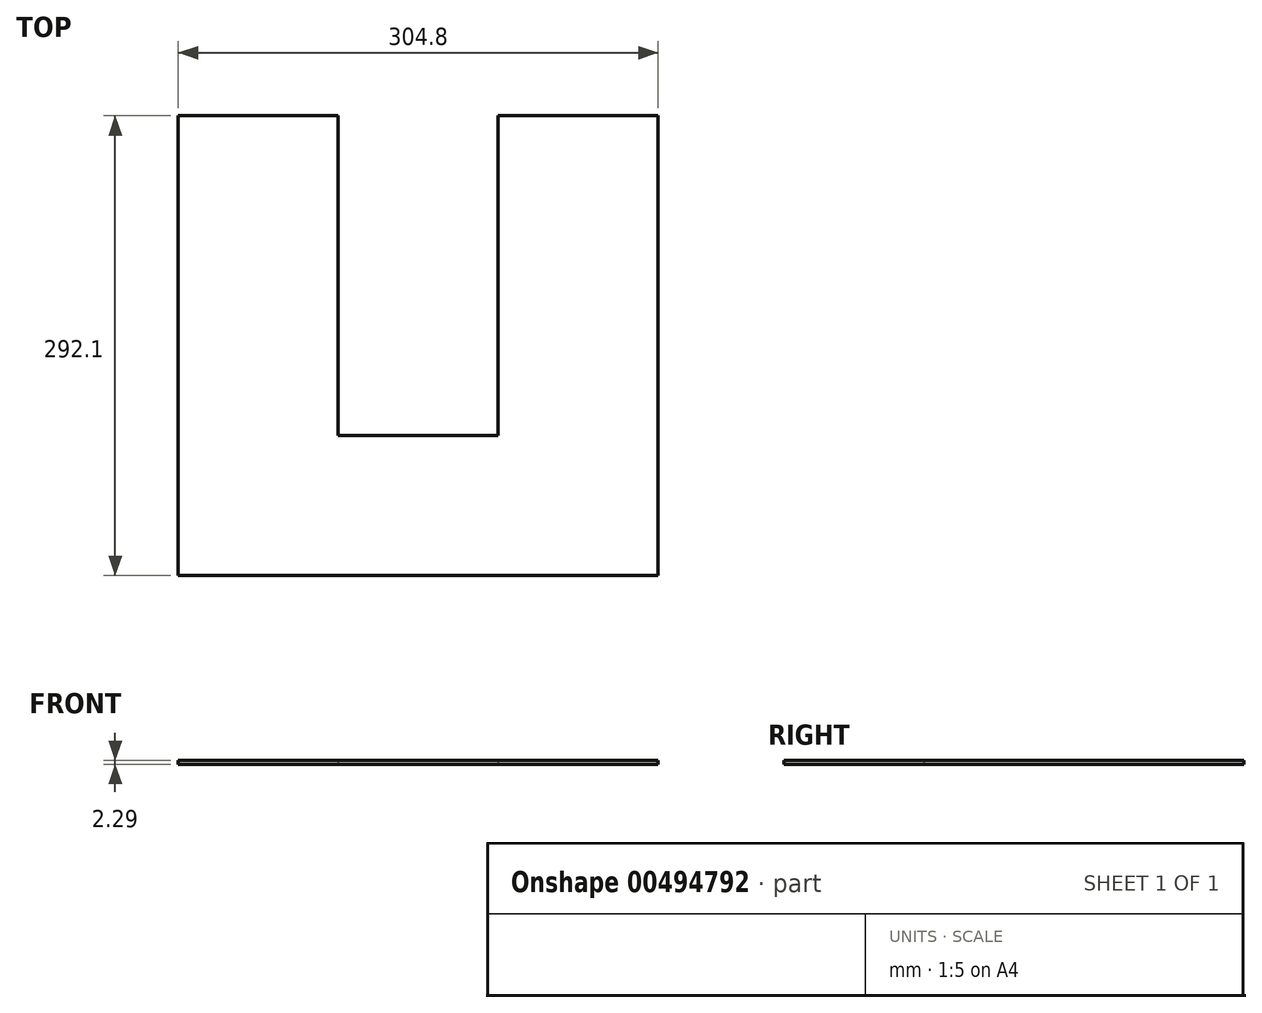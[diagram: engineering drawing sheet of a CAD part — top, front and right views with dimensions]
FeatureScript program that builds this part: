
annotation { "Feature Type Name" : "Feature", "Feature Type Description" : "" }
export const myFeature = defineFeature(function(context is Context, id is Id, definition is map)
    precondition{}
    {
        {
            var Q0;
            Q0=qCreatedBy(makeId("Top.planeOp"),FACE);
            var sketch = newSketch(context, id + "F0", { "sketchPlane" : qUnion([Q0])});
            skLineSegment(sketch, "E0.bottom", {"start": v(152.4, 146.05) * mm, "end": v(50.8, 146.05) * mm});
            skLineSegment(sketch, "E0.top", {"start": v(152.4, -146.05) * mm, "end": v(-152.4, -146.05) * mm});
            skLineSegment(sketch, "E0.left", {"start": v(152.4, 146.05) * mm, "end": v(152.4, -146.05) * mm});
            skLineSegment(sketch, "E0.right", {"start": v(-152.4, 146.05) * mm, "end": v(-152.4, -146.05) * mm});
            skPoint(sketch, "E0.middle", {"position": v(0, 0) * mm});
            skLineSegment(sketch, "E1.top", {"start": v(-50.8, -57.15) * mm, "end": v(50.8, -57.15) * mm});
            skLineSegment(sketch, "E1.left", {"start": v(-50.8, 146.05) * mm, "end": v(-50.8, -57.15) * mm});
            skLineSegment(sketch, "E1.right", {"start": v(50.8, 146.05) * mm, "end": v(50.8, -57.15) * mm});
            skLineSegment(sketch, "E2.trimOffspring", {"start": v(-50.8, 146.05) * mm, "end": v(-152.4, 146.05) * mm});
            skSolve(sketch);
        }
        {
            var Q0;
            Q0=makeQuery(id+"F0.imprint","IMPRINT",FACE,{"disambiguationData":[TD([[makeQuery(id+"F0.imprint","IMPRINT",EDGE,{"derivedFrom":sQuery(id+"F0.wireOp",EDGE,"E0.bottom")}),1.0]])]});
            extrude(context, id + "F1", {"entities" : qUnion([Q0]), "depth" : 2.3 * mm});
        }
    });
